# Revit family: Bicycle-Rack_Dero_Bike-File-Wall
name_source: partatom
category: Generic Models
units: mm (PartAtom-declared; Revit-internal decimal feet)

## family parameters
Can host rebar = No
Classification Number = 23.40.10.11.11
Cut with Voids When Loaded = No
Host = Face
Maintain Annotation Orientation = No
Part Type = Normal
Room Calculation Point = No
Round Connector Dimension = Use Diameter
Shared = No

## types (1)
- as Specified
    Assembly Code = E1090900
    Available Options = Galvanized
    CAD Details = https://www.arcat.com
    Capacity = 9 Bikes per Unit
    Cost = 0 $
    Default Elevation = 0' - 0"
    Description = Dero Wall Mounted Bike Rack - Bike File as Specified
    Keynote = 12 93 13
    Manufacturer = Dero Bike Rack Co.
    Model = Bike File Wall
    Mounting Height = 6' - 0"
    Product Page URL = https://www.arcat.com
    Specification = https://www.arcat.com
    URL = http://www.dero.com
    Unit Depth = 2' - 0"
    Unit Height = 2' - 0"
    Unit Width = 8' - 0"

## geometry (parser evidence)
native form markers: Sweep x12
no freeform markers — native parametric forms only
